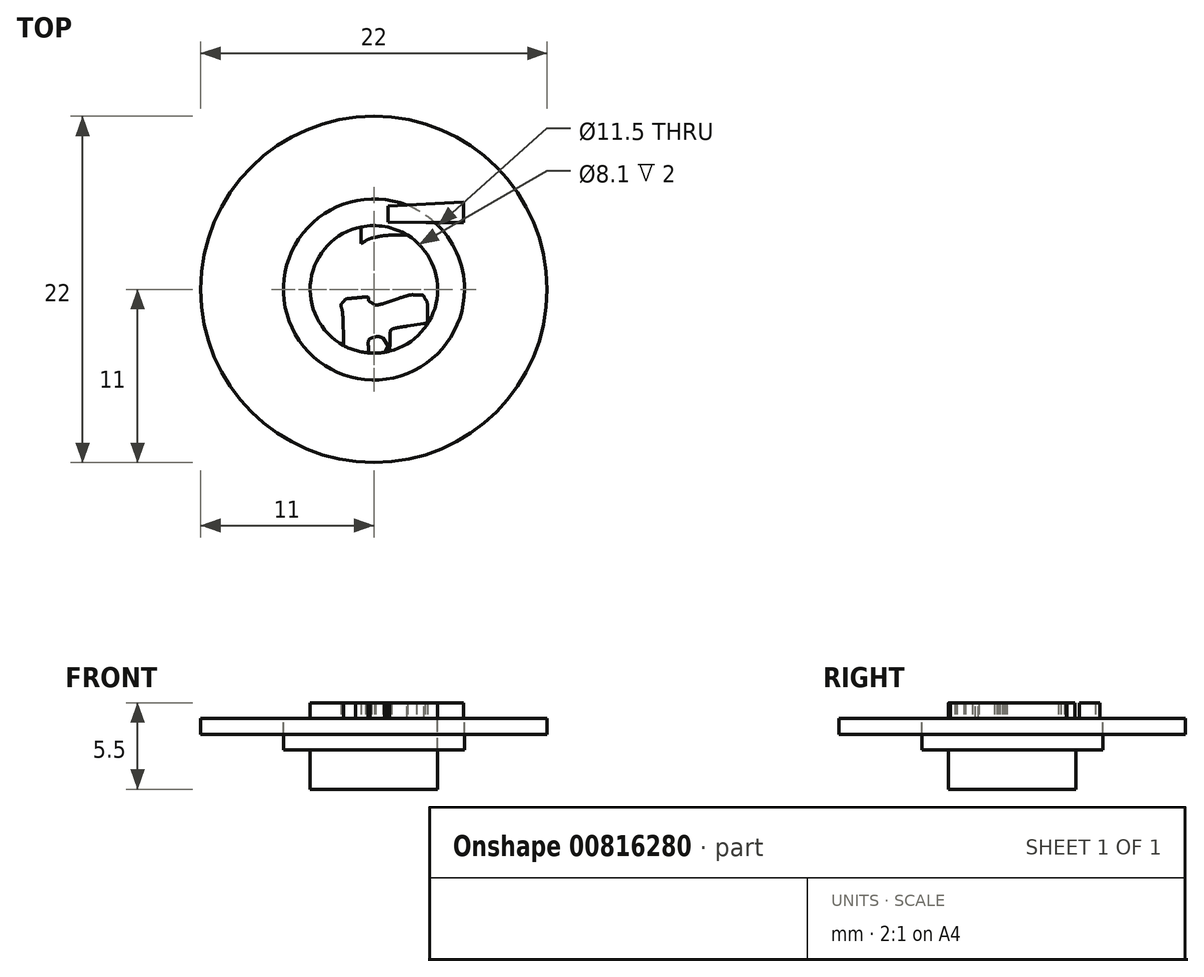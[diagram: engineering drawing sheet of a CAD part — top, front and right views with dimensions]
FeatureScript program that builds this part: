
annotation { "Feature Type Name" : "Feature", "Feature Type Description" : "" }
export const myFeature = defineFeature(function(context is Context, id is Id, definition is map)
    precondition{}
    {
        {
            var Q0;
            Q0=qCreatedBy(makeId("Top.planeOp"),FACE);
            var sketch = newSketch(context, id + "F0", { "sketchPlane" : qUnion([Q0])});
            skCircle(sketch, "E0", {"center": v(0, 0) * mm, "radius": 4.05 * mm});
            skCircle(sketch, "E1", {"center": v(0, 0) * mm, "radius": 5.75 * mm});
            skCircle(sketch, "E2", {"center": v(0, 0) * mm, "radius": 11 * mm});
            skSolve(sketch);
        }
        {
            var Q0;
            Q0=makeQuery(id+"F0.imprint","IMPRINT",FACE,{"disambiguationData":[TD([[makeQuery(id+"F0.imprint","IMPRINT",EDGE,{"derivedFrom":sQuery(id+"F0.wireOp",EDGE,"E0")}),-1.0]])]});
            extrude(context, id + "F1", {"entities" : qUnion([Q0]), "oppositeDirection" : true, "depth" : 2 * mm, "offsetDistance" : 25 * mm});
        }
        {
            var Q0;
            Q0=makeQuery(id+"F0.imprint","IMPRINT",FACE,{"disambiguationData":[TD([[makeQuery(id+"F0.imprint","IMPRINT",EDGE,{"derivedFrom":sQuery(id+"F0.wireOp",EDGE,"E1")}),-1.0]])]});
            extrude(context, id + "F2", {"entities" : qUnion([Q0]), "oppositeDirection" : true, "depth" : 1 * mm, "offsetDistance" : 25 * mm});
        }
        {
            var Q0;
            Q0=makeQuery(id+"F0.imprint","IMPRINT",FACE,{"disambiguationData":[TD([[makeQuery(id+"F0.imprint","IMPRINT",EDGE,{"derivedFrom":sQuery(id+"F0.wireOp",EDGE,"E0")}),1.0]])]});
            extrude(context, id + "F3", {"entities" : qUnion([Q0]), "oppositeDirection" : true, "depth" : 4.5 * mm, "offsetDistance" : 25 * mm});
        }
        {
            var Q0;
            Q0=makeQuery(id+"F0.imprint","IMPRINT",FACE,{"disambiguationData":[TD([[makeQuery(id+"F0.imprint","IMPRINT",EDGE,{"derivedFrom":sQuery(id+"F0.wireOp",EDGE,"E0")}),1.0]])]});
            var sketch = newSketch(context, id + "F4", { "sketchPlane" : qUnion([Q0])});
            skLineSegment(sketch, "E3", {"start": v(-5.48, 7.57) * mm, "end": v(-5.66, 7.14) * mm});
            skLineSegment(sketch, "E4", {"start": v(-5.66, 7.14) * mm, "end": v(-5.69, 0.15) * mm});
            skLineSegment(sketch, "E5", {"start": v(-5.69, 0.15) * mm, "end": v(-5.48, 7.57) * mm});
            skLineSegment(sketch, "E6", {"start": v(5.7, -2.62) * mm, "end": v(5.7, 1.76) * mm});
            skLineSegment(sketch, "E7", {"start": v(5.7, 1.76) * mm, "end": v(5.48, 2.06) * mm});
            skLineSegment(sketch, "E8", {"start": v(5.48, 2.06) * mm, "end": v(5.7, -2.62) * mm});
            skLineSegment(sketch, "E9", {"start": v(-0.54, 3.08) * mm, "end": v(-0.8, 2.93) * mm});
            skLineSegment(sketch, "E10", {"start": v(-0.8, 2.93) * mm, "end": v(-0.8, 4.61) * mm});
            skLineSegment(sketch, "E11", {"start": v(-0.8, 4.61) * mm, "end": v(-0.8, 6.3) * mm});
            skLineSegment(sketch, "E12", {"start": v(-0.8, 6.3) * mm, "end": v(-0.6, 6.42) * mm});
            skLineSegment(sketch, "E13", {"start": v(-0.6, 6.42) * mm, "end": v(-0.54, 3.08) * mm});
            skLineSegment(sketch, "E14", {"start": v(0.9, 5.3) * mm, "end": v(0.91, 4.28) * mm});
            skLineSegment(sketch, "E15", {"start": v(0.91, 4.28) * mm, "end": v(3.3, 4.26) * mm});
            skLineSegment(sketch, "E16", {"start": v(3.3, 4.26) * mm, "end": v(5.7, 4.25) * mm});
            skLineSegment(sketch, "E17", {"start": v(5.7, 4.25) * mm, "end": v(5.7, 5.56) * mm});
            skLineSegment(sketch, "E18", {"start": v(5.7, 5.56) * mm, "end": v(0.9, 5.3) * mm});
            skLineSegment(sketch, "E19", {"start": v(3.4, -1.48) * mm, "end": v(3.4, -2.12) * mm});
            skLineSegment(sketch, "E20", {"start": v(3.4, -2.12) * mm, "end": v(3.2, -2.16) * mm});
            skLineSegment(sketch, "E21", {"start": v(3.2, -2.16) * mm, "end": v(3.4, -1.48) * mm});
            skLineSegment(sketch, "E22", {"start": v(1.01, -3.41) * mm, "end": v(0.99, -4.21) * mm});
            skLineSegment(sketch, "E23", {"start": v(0.99, -4.21) * mm, "end": v(0.48, -4.32) * mm});
            skLineSegment(sketch, "E24", {"start": v(0.48, -4.32) * mm, "end": v(1.01, -3.41) * mm});
            skLineSegment(sketch, "E25", {"start": v(0.87, -3.53) * mm, "end": v(0.87, -3.15) * mm});
            skLineSegment(sketch, "E26", {"start": v(0.87, -3.15) * mm, "end": v(0.58, -3.07) * mm});
            skLineSegment(sketch, "E27", {"start": v(0.58, -3.07) * mm, "end": v(0.87, -3.53) * mm});
            skFitSpline(sketch, "E28", {"points": [v(-1.53, 9.99) * mm, v(-2.17, 9.9) * mm, v(-3.12, 9.65) * mm, v(-3.58, 9.45) * mm]});
            skFitSpline(sketch, "E29", {"points": [v(-3.58, 9.45) * mm, v(-4.5, 9.05) * mm, v(-5.1, 8.45) * mm, v(-5.48, 7.57) * mm]});
            skFitSpline(sketch, "E30", {"points": [v(-5.69, 0.15) * mm, v(-5.7, -5.9) * mm, v(-5.7, -6.9) * mm, v(-5.59, -7.32) * mm]});
            skFitSpline(sketch, "E31", {"points": [v(-5.59, -7.32) * mm, v(-5.27, -8.65) * mm, v(-4.3, -9.43) * mm, v(-2.45, -9.85) * mm]});
            skFitSpline(sketch, "E32", {"points": [v(-2.45, -9.85) * mm, v(-1.83, -9.99) * mm, v(-1.6, -10) * mm, v(-0.08, -10) * mm]});
            skFitSpline(sketch, "E33", {"points": [v(-0.08, -10) * mm, v(1.42, -10) * mm, v(1.67, -9.98) * mm, v(2.25, -9.85) * mm]});
            skFitSpline(sketch, "E34", {"points": [v(2.25, -9.85) * mm, v(4.08, -9.43) * mm, v(5.3, -8.5) * mm, v(5.6, -7.3) * mm]});
            skFitSpline(sketch, "E35", {"points": [v(5.6, -7.3) * mm, v(5.66, -7.12) * mm, v(5.7, -5.34) * mm, v(5.7, -2.62) * mm]});
            skFitSpline(sketch, "E36", {"points": [v(5.48, 2.06) * mm, v(5.04, 2.65) * mm, v(4.32, 3.07) * mm, v(3.36, 3.28) * mm]});
            skFitSpline(sketch, "E37", {"points": [v(3.36, 3.28) * mm, v(2.82, 3.4) * mm, v(0.7, 3.42) * mm, v(0.12, 3.31) * mm]});
            skFitSpline(sketch, "E38", {"points": [v(0.12, 3.31) * mm, v(-0.1, 3.27) * mm, v(-0.39, 3.17) * mm, v(-0.54, 3.08) * mm]});
            skFitSpline(sketch, "E39", {"points": [v(-0.6, 6.42) * mm, v(-0.33, 6.58) * mm, v(0.4, 6.58) * mm, v(0.67, 6.42) * mm]});
            skFitSpline(sketch, "E40", {"points": [v(0.67, 6.42) * mm, v(0.87, 6.3) * mm, v(0.87, 6.3) * mm, v(0.9, 5.3) * mm]});
            skFitSpline(sketch, "E41", {"points": [v(5.7, 5.56) * mm, v(5.7, 7.43) * mm, v(5.47, 8.09) * mm, v(4.62, 8.84) * mm]});
            skFitSpline(sketch, "E42", {"points": [v(4.62, 8.84) * mm, v(4.13, 9.28) * mm, v(3.53, 9.55) * mm, v(2.58, 9.8) * mm]});
            skFitSpline(sketch, "E43", {"points": [v(2.58, 9.8) * mm, v(1.96, 9.96) * mm, v(1.78, 9.98) * mm, v(0.3, 10) * mm]});
            skFitSpline(sketch, "E44", {"points": [v(0.3, 10) * mm, v(-0.58, 10) * mm, v(-1.4, 10) * mm, v(-1.53, 9.99) * mm]});
            skFitSpline(sketch, "E45", {"points": [v(3.26, -0.6) * mm, v(3.37, -0.77) * mm, v(3.4, -1) * mm, v(3.4, -1.48) * mm]});
            skFitSpline(sketch, "E46", {"points": [v(3.2, -2.16) * mm, v(3.07, -2.18) * mm, v(2.58, -2.26) * mm, v(2.1, -2.34) * mm]});
            skFitSpline(sketch, "E47", {"points": [v(2.1, -2.34) * mm, v(1.62, -2.4) * mm, v(1.18, -2.5) * mm, v(1.13, -2.54) * mm]});
            skFitSpline(sketch, "E48", {"points": [v(1.13, -2.54) * mm, v(1.07, -2.59) * mm, v(1.03, -2.88) * mm, v(1.01, -3.41) * mm]});
            skFitSpline(sketch, "E49", {"points": [v(0.48, -4.32) * mm, v(-0.39, -4.5) * mm, v(-0.35, -4.42) * mm, v(-0.35, -6.25) * mm]});
            skFitSpline(sketch, "E50", {"points": [v(-0.35, -6.25) * mm, v(-0.35, -7.43) * mm, v(-0.37, -7.84) * mm, v(-0.44, -7.89) * mm]});
            skFitSpline(sketch, "E51", {"points": [v(-0.44, -7.89) * mm, v(-0.57, -7.97) * mm, v(-1.2, -8.1) * mm, v(-1.49, -8.1) * mm]});
            skFitSpline(sketch, "E52", {"points": [v(-1.49, -8.1) * mm, v(-1.62, -8.1) * mm, v(-1.8, -8.03) * mm, v(-1.95, -7.93) * mm]});
            skFitSpline(sketch, "E53", {"points": [v(-1.95, -7.93) * mm, v(-2.15, -7.8) * mm, v(-2.17, -7.74) * mm, v(-2.1, -7.64) * mm]});
            skFitSpline(sketch, "E54", {"points": [v(-2.1, -7.64) * mm, v(-2.02, -7.5) * mm, v(-2, -1.47) * mm, v(-2.08, -1.13) * mm]});
            skFitSpline(sketch, "E55", {"points": [v(-2.08, -1.13) * mm, v(-2.1, -1.02) * mm, v(-2.05, -0.9) * mm, v(-1.94, -0.78) * mm]});
            skFitSpline(sketch, "E56", {"points": [v(-1.94, -0.78) * mm, v(-1.79, -0.62) * mm, v(-1.69, -0.59) * mm, v(-1.16, -0.54) * mm]});
            skFitSpline(sketch, "E57", {"points": [v(-1.16, -0.54) * mm, v(-0.5, -0.48) * mm, v(-0.35, -0.5) * mm, v(-0.35, -0.64) * mm]});
            skFitSpline(sketch, "E58", {"points": [v(-0.35, -0.64) * mm, v(-0.35, -0.69) * mm, v(-0.26, -0.78) * mm, v(-0.16, -0.84) * mm]});
            skFitSpline(sketch, "E59", {"points": [v(-0.16, -0.84) * mm, v(0.1, -0.99) * mm, v(0.48, -0.93) * mm, v(1.49, -0.6) * mm]});
            skFitSpline(sketch, "E60", {"points": [v(1.49, -0.6) * mm, v(2.12, -0.4) * mm, v(2.38, -0.34) * mm, v(2.71, -0.36) * mm]});
            skFitSpline(sketch, "E61", {"points": [v(2.71, -0.36) * mm, v(3.1, -0.37) * mm, v(3.14, -0.38) * mm, v(3.26, -0.6) * mm]});
            skFitSpline(sketch, "E62", {"points": [v(0.03, -3.04) * mm, v(-0.25, -3.13) * mm, v(-0.35, -3.28) * mm, v(-0.35, -3.62) * mm]});
            skFitSpline(sketch, "E63", {"points": [v(-0.35, -3.62) * mm, v(-0.35, -3.8) * mm, v(-0.31, -4) * mm, v(-0.26, -4.04) * mm]});
            skFitSpline(sketch, "E64", {"points": [v(-0.26, -4.04) * mm, v(-0.2, -4.09) * mm, v(0.04, -4.12) * mm, v(0.3, -4.12) * mm]});
            skFitSpline(sketch, "E65", {"points": [v(0.3, -4.12) * mm, v(0.86, -4.12) * mm, v(0.87, -4.1) * mm, v(0.87, -3.53) * mm]});
            skFitSpline(sketch, "E66", {"points": [v(0.58, -3.07) * mm, v(0.26, -2.99) * mm, v(0.2, -2.99) * mm, v(0.03, -3.04) * mm]});
            skSolve(sketch);
        }
        {
            var Q0;
            Q0=makeQuery(id+"F4.imprint","IMPRINT",FACE,{"disambiguationData":[TD([[makeQuery(id+"F4.imprint","IMPRINT",EDGE,{"derivedFrom":sQuery(id+"F4.wireOp",EDGE,"E5")}),-1.0]])]});
            var Q1;
            Q1=makeQuery(id+"F4.imprint","IMPRINT",FACE,{"disambiguationData":[TD([[makeQuery(id+"F4.imprint","IMPRINT",EDGE,{"derivedFrom":sQuery(id+"F4.wireOp",EDGE,"E14")}),1.0]])]});
            var Q2;
            {var subQ5=sQuery(id+"F4.wireOp",EDGE,"E9");Q2=makeQuery(id+"F4.imprint","IMPRINT",FACE,{"disambiguationData":[TD([[makeQuery(id+"F4.imprint","IMPRINT",EDGE,{"derivedFrom":subQ5}),1.0]])]});}
            var Q3;
            {var subQ4=sQuery(id+"F4.wireOp",EDGE,"E27");Q3=makeQuery(id+"F4.imprint","IMPRINT",FACE,{"disambiguationData":[TD([[makeQuery(id+"F4.imprint","IMPRINT",EDGE,{"derivedFrom":subQ4}),-1.0]])]});}
            extrude(context, id + "F5", {"entities" : qUnion([Q0, Q1, Q2, Q3]), "depth" : 1 * mm, "offsetDistance" : 25 * mm});
        }
    });
